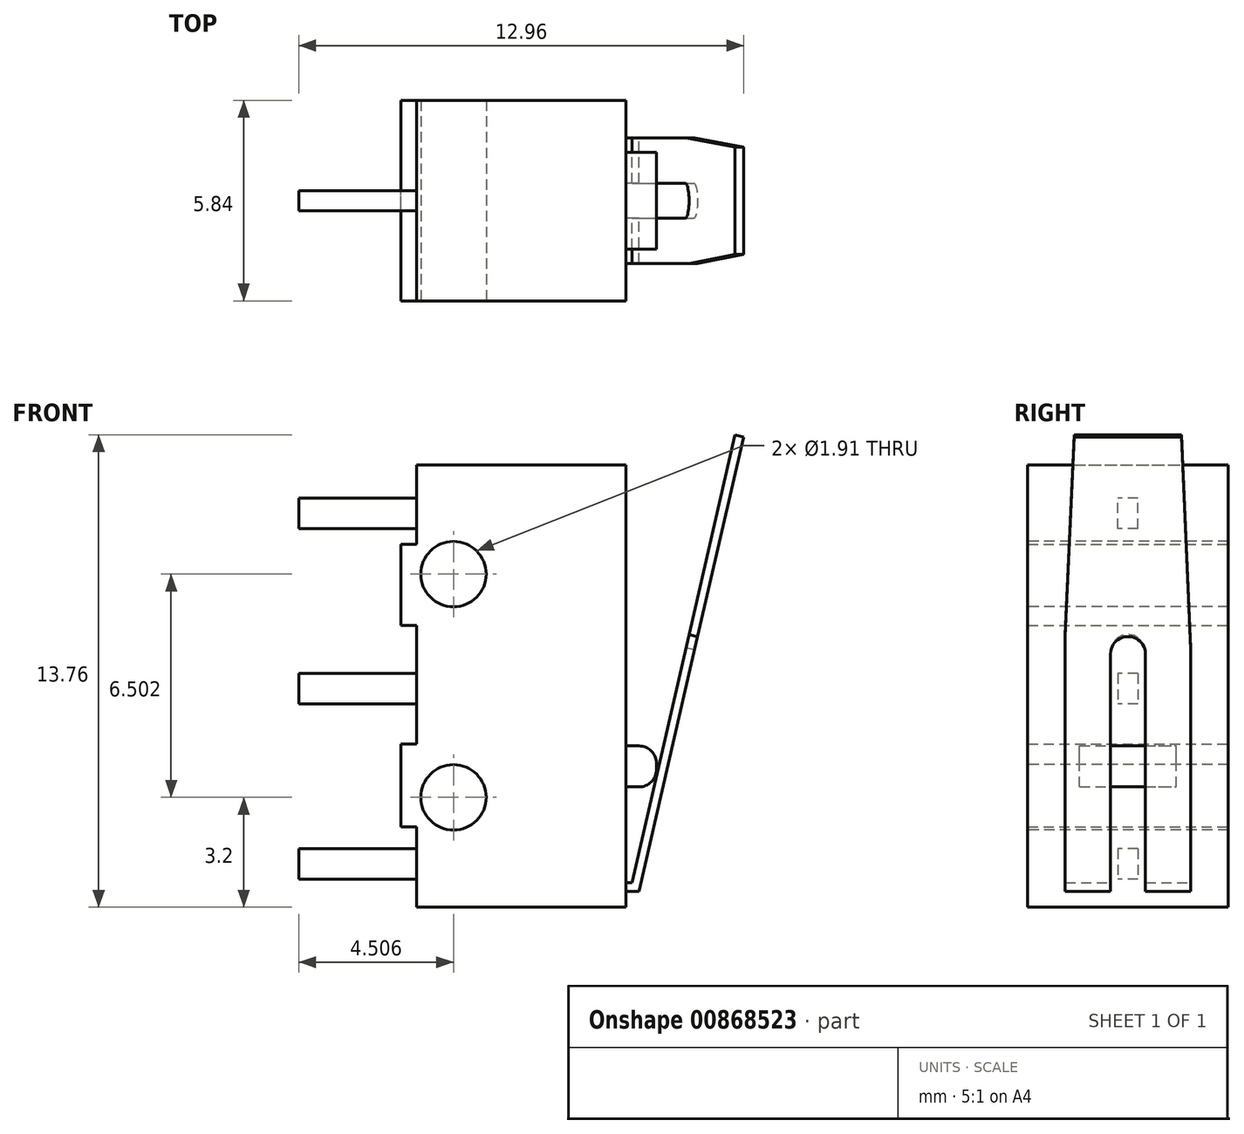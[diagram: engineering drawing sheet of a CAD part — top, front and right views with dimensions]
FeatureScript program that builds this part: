
annotation { "Feature Type Name" : "Feature", "Feature Type Description" : "" }
export const myFeature = defineFeature(function(context is Context, id is Id, definition is map)
    precondition{}
    {
        {
            var Q0;
            Q0=qCreatedBy(makeId("Front.planeOp"),FACE);
            var sketch = newSketch(context, id + "F0", { "sketchPlane" : qUnion([Q0])});
            skLineSegment(sketch, "E0.bottom", {"start": v(0, 0) * mm, "end": v(6.1, 0) * mm});
            skLineSegment(sketch, "E0.top", {"start": v(0, 12.88) * mm, "end": v(6.1, 12.88) * mm});
            skLineSegment(sketch, "E0.left", {"start": v(0, 0) * mm, "end": v(0, 2.34) * mm});
            skLineSegment(sketch, "E0.right", {"start": v(6.1, 0) * mm, "end": v(6.1, 12.88) * mm});
            skLineSegment(sketch, "E1", {"start": v(-0.46, 10.57) * mm, "end": v(-0.46, 8.2) * mm});
            skLineSegment(sketch, "E2", {"start": v(-0.46, 10.57) * mm, "end": v(0, 10.57) * mm});
            skLineSegment(sketch, "E3", {"start": v(-0.46, 2.34) * mm, "end": v(0, 2.34) * mm});
            skLineSegment(sketch, "E4", {"start": v(-0.46, 4.75) * mm, "end": v(0, 4.75) * mm});
            skLineSegment(sketch, "E5", {"start": v(-0.46, 8.2) * mm, "end": v(0, 8.2) * mm});
            skLineSegment(sketch, "E6.trimOffspring", {"start": v(-0.46, 4.75) * mm, "end": v(-0.46, 2.34) * mm});
            skLineSegment(sketch, "E7.trimOffspring", {"start": v(0, 10.57) * mm, "end": v(0, 12.88) * mm});
            skLineSegment(sketch, "E8.trimOffspring", {"start": v(0, 4.75) * mm, "end": v(0, 8.2) * mm});
            skSolve(sketch);
        }
        {
            var Q0;
            Q0 = qSketchRegion(id + "F0", true);
            extrude(context, id + "F1", {"entities" : qUnion([Q0]), "depth" : 5.84 * mm, "offsetDistance" : 25.4 * mm});
        }
        {
            var Q0;
            Q0=makeQuery(id+"F1.opExtrude","CAP_FACE",FACE,{"disambiguationData":[OSD([sQuery(id+"F0.wireOp",EDGE,"E0.bottom"),sQuery(id+"F0.wireOp",EDGE,"E0.top"),sQuery(id+"F0.wireOp",EDGE,"E0.left"),sQuery(id+"F0.wireOp",EDGE,"E0.right"),sQuery(id+"F0.wireOp",EDGE,"E1"),sQuery(id+"F0.wireOp",EDGE,"E2"),sQuery(id+"F0.wireOp",EDGE,"E3"),sQuery(id+"F0.wireOp",EDGE,"E4"),sQuery(id+"F0.wireOp",EDGE,"E5"),sQuery(id+"F0.wireOp",EDGE,"E6.trimOffspring"),sQuery(id+"F0.wireOp",EDGE,"E7.trimOffspring"),sQuery(id+"F0.wireOp",EDGE,"E8.trimOffspring")])],"isStart":false});
            var sketch = newSketch(context, id + "F2", { "sketchPlane" : qUnion([Q0])});
            skCircle(sketch, "E9", {"center": v(1.08, 9.7) * mm, "radius": 0.95 * mm});
            skCircle(sketch, "E10", {"center": v(1.08, 3.2) * mm, "radius": 0.95 * mm});
            skSolve(sketch);
        }
        {
            var Q0;
            Q0 = qSketchRegion(id + "F2", true);
            extrude(context, id + "F3", {"entities" : qUnion([Q0]), "operationType" : NewBodyOperationType.REMOVE, "oppositeDirection" : true, "depth" : 25.4 * mm, "offsetDistance" : 25.4 * mm});
        }
        {
            var Q0;
            Q0=qCreatedBy(makeId("Front.planeOp"),FACE);
            cPlane(context, id + "F4", {"entities" : qUnion([Q0]), "cplaneType" : CPlaneType.OFFSET, "offset" : 2.92 * mm, "width" : 152.4 * mm, "height" : 152.4 * mm});
        }
        {
            var Q0;
            Q0=qCreatedBy(id+"F4.planeOp",FACE);
            var sketch = newSketch(context, id + "F5", { "sketchPlane" : qUnion([Q0])});
            skLineSegment(sketch, "E11.bottom", {"start": v(6.1, 3.5) * mm, "end": v(6.99, 3.5) * mm});
            skLineSegment(sketch, "E11.top", {"start": v(6.1, 4.7) * mm, "end": v(6.99, 4.7) * mm});
            skLineSegment(sketch, "E11.left", {"start": v(6.1, 3.5) * mm, "end": v(6.1, 4.7) * mm});
            skLineSegment(sketch, "E11.right", {"start": v(6.99, 3.5) * mm, "end": v(6.99, 4.7) * mm});
            skSolve(sketch);
        }
        {
            var Q0;
            Q0 = qSketchRegion(id + "F5", true);
            extrude(context, id + "F6", {"entities" : qUnion([Q0]), "operationType" : NewBodyOperationType.ADD, "endBound" : BoundingType.SYMMETRIC, "depth" : 2.82 * mm, "offsetDistance" : 25.4 * mm});
        }
        {
            var Q0;
            Q0=makeQuery(id+"F6.opExtrude","SWEPT_EDGE",EDGE,{"disambiguationData":[OSD([sQuery(id+"F5.wireOp",EDGE,"E11.top"),sQuery(id+"F5.wireOp",EDGE,"E11.right")])]});
            var Q1;
            Q1=makeQuery(id+"F6.opExtrude","SWEPT_EDGE",EDGE,{"disambiguationData":[OSD([sQuery(id+"F5.wireOp",EDGE,"E11.bottom"),sQuery(id+"F5.wireOp",EDGE,"E11.right")])]});
            fillet(context, id + "F7", {"entities" : qUnion([Q0, Q1]), "radius" : 0.5 * mm, "tangentPropagation" : true, "allowEdgeOverflow" : false});
        }
        {
            var Q0;
            Q0=qCreatedBy(id+"F4.planeOp",FACE);
            var sketch = newSketch(context, id + "F8", { "sketchPlane" : qUnion([Q0])});
            skLineSegment(sketch, "E12", {"start": v(6.1, 0.46) * mm, "end": v(6.48, 0.46) * mm});
            skLineSegment(sketch, "E13", {"start": v(6.48, 0.46) * mm, "end": v(9.53, 13.7) * mm});
            skLineSegment(sketch, "E14", {"start": v(9.53, 13.7) * mm, "end": v(9.28, 13.76) * mm});
            skLineSegment(sketch, "E15", {"start": v(9.28, 13.76) * mm, "end": v(6.27, 0.71) * mm});
            skLineSegment(sketch, "E16", {"start": v(6.1, 0.46) * mm, "end": v(6.1, 0.71) * mm});
            skLineSegment(sketch, "E17", {"start": v(6.1, 0.71) * mm, "end": v(6.27, 0.71) * mm});
            skSolve(sketch);
        }
        {
            var Q0;
            Q0 = qSketchRegion(id + "F8", true);
            extrude(context, id + "F9", {"entities" : qUnion([Q0]), "operationType" : NewBodyOperationType.ADD, "endBound" : BoundingType.SYMMETRIC, "depth" : 3.66 * mm, "offsetDistance" : 25.4 * mm});
        }
        {
            var Q0;
            Q0=makeQuery(id+"F9.opExtrude","SWEPT_FACE",FACE,{"disambiguationData":[OSD([sQuery(id+"F8.wireOp",EDGE,"E13")])]});
            var sketch = newSketch(context, id + "F10", { "sketchPlane" : qUnion([Q0])});
            skLineSegment(sketch, "E18", {"start": v(-4.48, 15.49) * mm, "end": v(-4.75, 9.52) * mm});
            skLineSegment(sketch, "E19", {"start": v(-4.75, 9.52) * mm, "end": v(-4.75, 15.49) * mm});
            skLineSegment(sketch, "E20", {"start": v(-4.75, 15.49) * mm, "end": v(-4.48, 15.49) * mm});
            skLineSegment(sketch, "E21", {"start": v(-1.1, 15.49) * mm, "end": v(-1.36, 15.49) * mm});
            skLineSegment(sketch, "E22", {"start": v(-1.36, 15.49) * mm, "end": v(-1.1, 9.14) * mm});
            skLineSegment(sketch, "E23", {"start": v(-1.1, 9.14) * mm, "end": v(-1.1, 15.49) * mm});
            skLineSegment(sketch, "E24.bottom", {"start": v(-3.43, 1.9) * mm, "end": v(-2.41, 1.9) * mm});
            skLineSegment(sketch, "E24.top", {"start": v(-2.92, 9.52) * mm, "end": v(-2.92, 9.52) * mm});
            skLineSegment(sketch, "E24.left", {"start": v(-3.43, 1.9) * mm, "end": v(-3.43, 9.01) * mm});
            skLineSegment(sketch, "E24.right", {"start": v(-2.41, 1.9) * mm, "end": v(-2.41, 9.01) * mm});
            skPoint(sketch, "E25.visualSharp", {"position": v(-3.43, 9.52) * mm});
            skArc(sketch, "E25.filletArc", {"start": v(-2.92, 9.52) * mm, "mid": v(-3.28, 9.37) * mm, "end": v(-3.43, 9.01) * mm});
            skPoint(sketch, "E26.visualSharp", {"position": v(-2.41, 9.52) * mm});
            skArc(sketch, "E26.filletArc", {"start": v(-2.41, 9.01) * mm, "mid": v(-2.56, 9.37) * mm, "end": v(-2.92, 9.52) * mm});
            skSolve(sketch);
        }
        {
            var Q0;
            Q0 = qSketchRegion(id + "F10", true);
            extrude(context, id + "F11", {"entities" : qUnion([Q0]), "operationType" : NewBodyOperationType.REMOVE, "oppositeDirection" : true, "depth" : 0.25 * mm, "offsetDistance" : 25.4 * mm});
        }
        {
            var Q0;
            Q0=makeQuery(id+"F1.opExtrude","SWEPT_FACE",FACE,{"disambiguationData":[OSD([sQuery(id+"F0.wireOp",EDGE,"E0.right")])]});
            var sketch = newSketch(context, id + "F12", { "sketchPlane" : qUnion([Q0])});
            skLineSegment(sketch, "E27.bottom", {"start": v(-3.43, 1.1) * mm, "end": v(-2.41, 1.1) * mm});
            skLineSegment(sketch, "E27.top", {"start": v(-3.43, 0.17) * mm, "end": v(-2.41, 0.17) * mm});
            skLineSegment(sketch, "E27.left", {"start": v(-3.43, 1.1) * mm, "end": v(-3.43, 0.17) * mm});
            skLineSegment(sketch, "E27.right", {"start": v(-2.41, 1.1) * mm, "end": v(-2.41, 0.17) * mm});
            skSolve(sketch);
        }
        {
            var Q0;
            Q0 = qSketchRegion(id + "F12", true);
            extrude(context, id + "F13", {"entities" : qUnion([Q0]), "operationType" : NewBodyOperationType.REMOVE, "depth" : 25.4 * mm, "offsetDistance" : 25.4 * mm});
        }
        {
            var Q0;
            Q0=makeQuery(id+"F1.opExtrude","SWEPT_FACE",FACE,{"disambiguationData":[OSD([sQuery(id+"F0.wireOp",EDGE,"E8.trimOffspring")])]});
            var sketch = newSketch(context, id + "F14", { "sketchPlane" : qUnion([Q0])});
            skLineSegment(sketch, "E28.bottom", {"start": v(2.63, 6.8) * mm, "end": v(3.21, 6.8) * mm});
            skLineSegment(sketch, "E28.top", {"start": v(2.63, 5.92) * mm, "end": v(3.21, 5.92) * mm});
            skLineSegment(sketch, "E28.left", {"start": v(2.63, 6.8) * mm, "end": v(2.63, 5.92) * mm});
            skLineSegment(sketch, "E28.right", {"start": v(3.21, 6.8) * mm, "end": v(3.21, 5.92) * mm});
            skLineSegment(sketch, "E29.bottom", {"start": v(2.63, 11.02) * mm, "end": v(3.21, 11.02) * mm});
            skLineSegment(sketch, "E29.top", {"start": v(2.63, 11.91) * mm, "end": v(3.21, 11.91) * mm});
            skLineSegment(sketch, "E29.left", {"start": v(2.63, 11.02) * mm, "end": v(2.63, 11.91) * mm});
            skLineSegment(sketch, "E29.right", {"start": v(3.21, 11.02) * mm, "end": v(3.21, 11.91) * mm});
            skPoint(sketch, "E30.firstSnap0", {"position": v(2.63, 6.36) * mm});
            skLineSegment(sketch, "E30.bottom", {"start": v(2.63, 1.7) * mm, "end": v(3.21, 1.7) * mm});
            skLineSegment(sketch, "E30.top", {"start": v(2.63, 0.81) * mm, "end": v(3.21, 0.81) * mm});
            skLineSegment(sketch, "E30.left", {"start": v(2.63, 1.7) * mm, "end": v(2.63, 0.81) * mm});
            skLineSegment(sketch, "E30.right", {"start": v(3.21, 1.7) * mm, "end": v(3.21, 0.81) * mm});
            skSolve(sketch);
        }
        {
            var Q0;
            Q0 = qSketchRegion(id + "F14", true);
            extrude(context, id + "F15", {"entities" : qUnion([Q0]), "operationType" : NewBodyOperationType.ADD, "depth" : 3.43 * mm, "offsetDistance" : 25.4 * mm});
        }
    });
